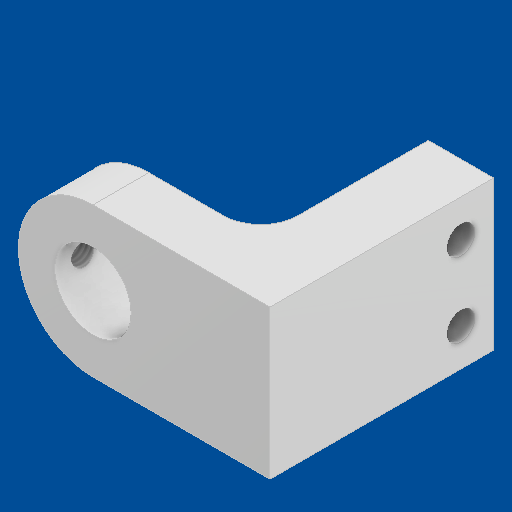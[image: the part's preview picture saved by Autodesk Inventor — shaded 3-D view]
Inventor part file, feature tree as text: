
AUTODESK INVENTOR PART (.ipt)
format: ipt  version: 2025 (Build 290162000, 162)  size: 216,576 bytes
history: native  units: in
note: dims shown in document units (in); Inventor stores cm internally (conversion verified against a paired STEP export)
features: direct_edit x11, move_body x8, other x6, hole x1, sketch x1
ambient origin geometry x8: Origin, YZ Plane, XZ Plane, XY Plane, X Axis, Y Axis, Z Axis, Center Point
bodies: Solid1 (feature_tree), Body3 (feature_tree)
feature tree (27):
  move_body  "Move Body1"
  direct_edit  "Direct Edit1"
  direct_edit  "Direct Edit2"
  direct_edit  "Direct Edit3"
  hole  "Hole1"  [1 undecoded]
  direct_edit  "Direct Edit4"
  direct_edit  "Direct Edit5"
  direct_edit  "Direct Edit6"
  direct_edit  "Direct Edit7"
  direct_edit  "Direct Edit8"
  direct_edit  "Direct Edit9"
  direct_edit  "Direct Edit10"
  direct_edit  "Direct Edit11"
  sketch  "Sketch1"  dims[d0=45.0deg d1=0.0059in d2=0.0625in d3=0.0625in d4=0.1181in d5=0.0in d6=0.0089in d7=90.0deg d8=0.0968in d9=0.2362in d10=0.1575in d11=0.0787in d12=90.0deg d13=0.3465in d14=0.8108in d15=0.0039in d16=0.0039in d17=0.0in d18=0.0in d19=-0.0295in d20=0.0in d21=0.0in d22=-0.0089in d23=0.0in d24=0.0in d25=-0.0089in d26=-0.0039in d27=0.0016in d28=0.0in d29=0.0in d30=-0.0083in d31=0.0in d32=0.0in d33=0.0in d34=0.0055in d35=0.0in d36=-0.0002in d37=0.0in d38=0.0in]
  other  "Size1"
  other  "Size2"
  other  "Size3"
  other  "Size4"
  other  "Size5"
  move_body  "Move1"
  move_body  "Move2"
  move_body  "Move3"
  other  "Size6"
  move_body  "Move4"
  move_body  "Move5"
  move_body  "Move6"
  move_body  "Move7"
note: 1 required parameter value undecoded (feature->parameter linkage not recoverable at this tier; creation-order binding heuristic only, values carry confidence <= 0.55)
